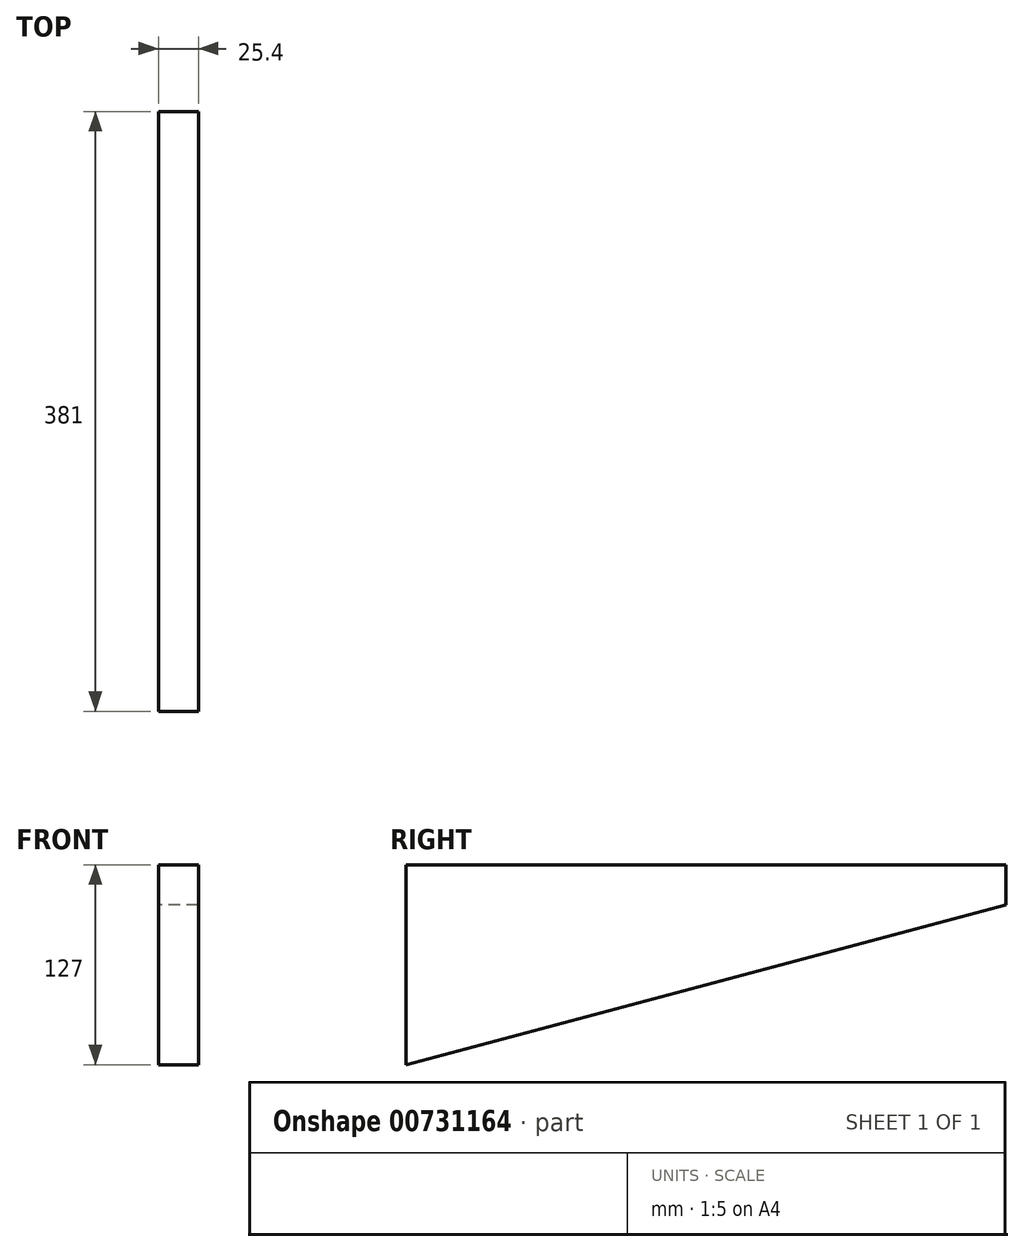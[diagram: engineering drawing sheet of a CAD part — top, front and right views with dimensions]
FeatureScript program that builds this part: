
annotation { "Feature Type Name" : "Feature", "Feature Type Description" : "" }
export const myFeature = defineFeature(function(context is Context, id is Id, definition is map)
    precondition{}
    {
        {
            var Q0;
            Q0=qCreatedBy(makeId("Right.planeOp"),FACE);
            var sketch = newSketch(context, id + "F0", { "sketchPlane" : qUnion([Q0])});
            skLineSegment(sketch, "E0.bottom", {"start": v(-190.5, -63.5) * mm, "end": v(190.5, -63.5) * mm});
            skLineSegment(sketch, "E0.top", {"start": v(-190.5, 63.5) * mm, "end": v(190.5, 63.5) * mm});
            skLineSegment(sketch, "E0.left", {"start": v(-190.5, -63.5) * mm, "end": v(-190.5, 63.5) * mm});
            skLineSegment(sketch, "E0.right", {"start": v(190.5, -63.5) * mm, "end": v(190.5, 63.5) * mm});
            skPoint(sketch, "E0.middle", {"position": v(0, 0) * mm});
            skLineSegment(sketch, "E1", {"start": v(-190.5, -63.5) * mm, "end": v(190.5, 38.1) * mm});
            skSolve(sketch);
        }
        {
            var Q0;
            {var subQ0=sQuery(id+"F0.wireOp",EDGE,"E0.top");Q0=makeQuery(id+"F0.imprint","IMPRINT",FACE,{"disambiguationData":[TD([[makeQuery(id+"F0.imprint","IMPRINT",EDGE,{"derivedFrom":subQ0}),-1.0]])]});}
            extrude(context, id + "F1", {"entities" : qUnion([Q0]), "depth" : 25.4 * mm, "offsetDistance" : 25.4 * mm});
        }
    });
